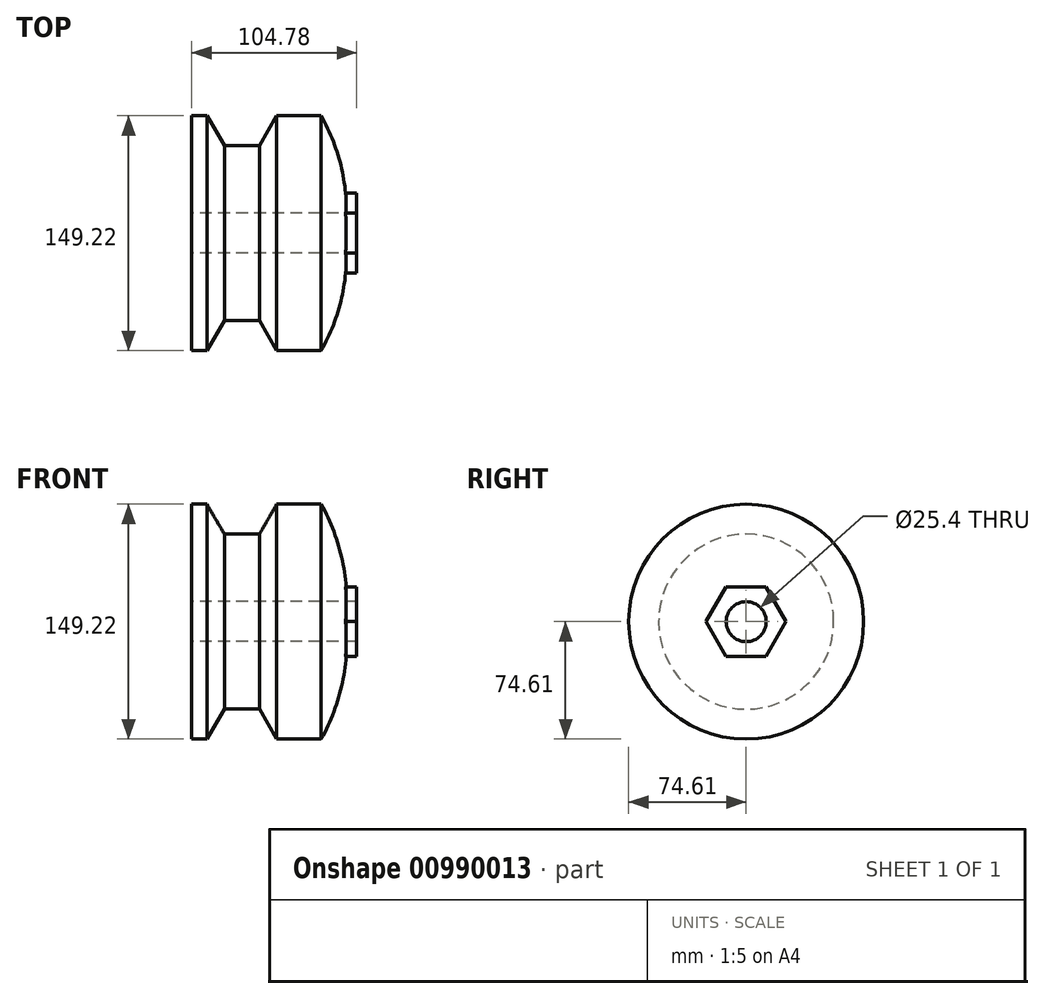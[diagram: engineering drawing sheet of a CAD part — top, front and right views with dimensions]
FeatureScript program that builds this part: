
annotation { "Feature Type Name" : "Feature", "Feature Type Description" : "" }
export const myFeature = defineFeature(function(context is Context, id is Id, definition is map)
    precondition{}
    {
        {
            var Q0;
            Q0=qCreatedBy(makeId("Front.planeOp"),FACE);
            var sketch = newSketch(context, id + "F0", { "sketchPlane" : qUnion([Q0])});
            skLineSegment(sketch, "E0", {"start": v(0, 74.61) * mm, "end": v(9.75, 74.61) * mm});
            skLineSegment(sketch, "E1", {"start": v(9.75, 74.61) * mm, "end": v(20.75, 55.56) * mm});
            skLineSegment(sketch, "E2", {"start": v(20.75, 55.56) * mm, "end": v(42.98, 55.56) * mm});
            skLineSegment(sketch, "E3", {"start": v(42.98, 55.56) * mm, "end": v(53.98, 74.61) * mm});
            skLineSegment(sketch, "E4", {"start": v(53.98, 74.61) * mm, "end": v(82.31, 74.61) * mm});
            skLineSegment(sketch, "E5", {"start": v(0, 0) * mm, "end": v(98.43, 0) * mm, "construction": true});
            skLineSegment(sketch, "E6", {"start": v(31.86, 55.56) * mm, "end": v(31.86, 0) * mm, "construction": true});
            skLineSegment(sketch, "E7.top", {"start": v(0, 12.7) * mm, "end": v(98.43, 12.7) * mm});
            skArc(sketch, "E8.trimOffspring", {"start": v(98.43, 12.7) * mm, "mid": v(94.33, 44.69) * mm, "end": v(82.31, 74.61) * mm});
            skLineSegment(sketch, "E9", {"start": v(98.43, 0) * mm, "end": v(98.43, 12.7) * mm, "construction": true});
            skLineSegment(sketch, "E10", {"start": v(0, 74.61) * mm, "end": v(0, 12.7) * mm});
            skSolve(sketch);
        }
        {
            var Q0;
            Q0=makeQuery(id+"F0.imprint","IMPRINT",FACE,{"disambiguationData":[TD([[makeQuery(id+"F0.imprint","IMPRINT",EDGE,{"derivedFrom":sQuery(id+"F0.wireOp",EDGE,"E0")}),-1.0]])]});
            var Q1;
            Q1=sQuery(id+"F0.wireOp",EDGE,"E5");
            revolve(context, id + "F1", {"surfaceOperationType" : NewSurfaceOperationType.NEW, "entities" : qUnion([Q0]), "axis" : qUnion([Q1]), "revolveType" : RevolveType.FULL});
        }
        {
            var Q0;
            Q0=qCreatedBy(makeId("Right.planeOp"),FACE);
            cPlane(context, id + "F2", {"entities" : qUnion([Q0]), "cplaneType" : CPlaneType.OFFSET, "offset" : 76.2 * mm, "width" : 152.4 * mm, "height" : 152.4 * mm});
        }
        {
            var Q0;
            Q0=qCreatedBy(id+"F2.planeOp",FACE);
            var sketch = newSketch(context, id + "F3", { "sketchPlane" : qUnion([Q0])});
            skCircle(sketch, "E11.cCircle", {"center": v(0, 0) * mm, "radius": 25.4 * mm, "construction": true});
            skLineSegment(sketch, "E11.0", {"start": v(12.7, 22) * mm, "end": v(25.4, 0) * mm});
            skLineSegment(sketch, "E11.1", {"start": v(25.4, 0) * mm, "end": v(12.7, -22) * mm});
            skLineSegment(sketch, "E11.2", {"start": v(12.7, -22) * mm, "end": v(-12.7, -22) * mm});
            skLineSegment(sketch, "E11.3", {"start": v(-12.7, -22) * mm, "end": v(-25.4, 0) * mm});
            skLineSegment(sketch, "E11.4", {"start": v(-25.4, 0) * mm, "end": v(-12.7, 22) * mm});
            skLineSegment(sketch, "E11.5", {"start": v(-12.7, 22) * mm, "end": v(12.7, 22) * mm});
            skCircle(sketch, "E12", {"center": v(0, 0) * mm, "radius": 12.7 * mm});
            skSolve(sketch);
        }
        {
            var Q0;
            Q0 = qSketchRegion(id + "F3", true);
            extrude(context, id + "F4", {"entities" : qUnion([Q0]), "operationType" : NewBodyOperationType.ADD, "depth" : 28.57 * mm, "offsetDistance" : 25.4 * mm});
        }
    });
